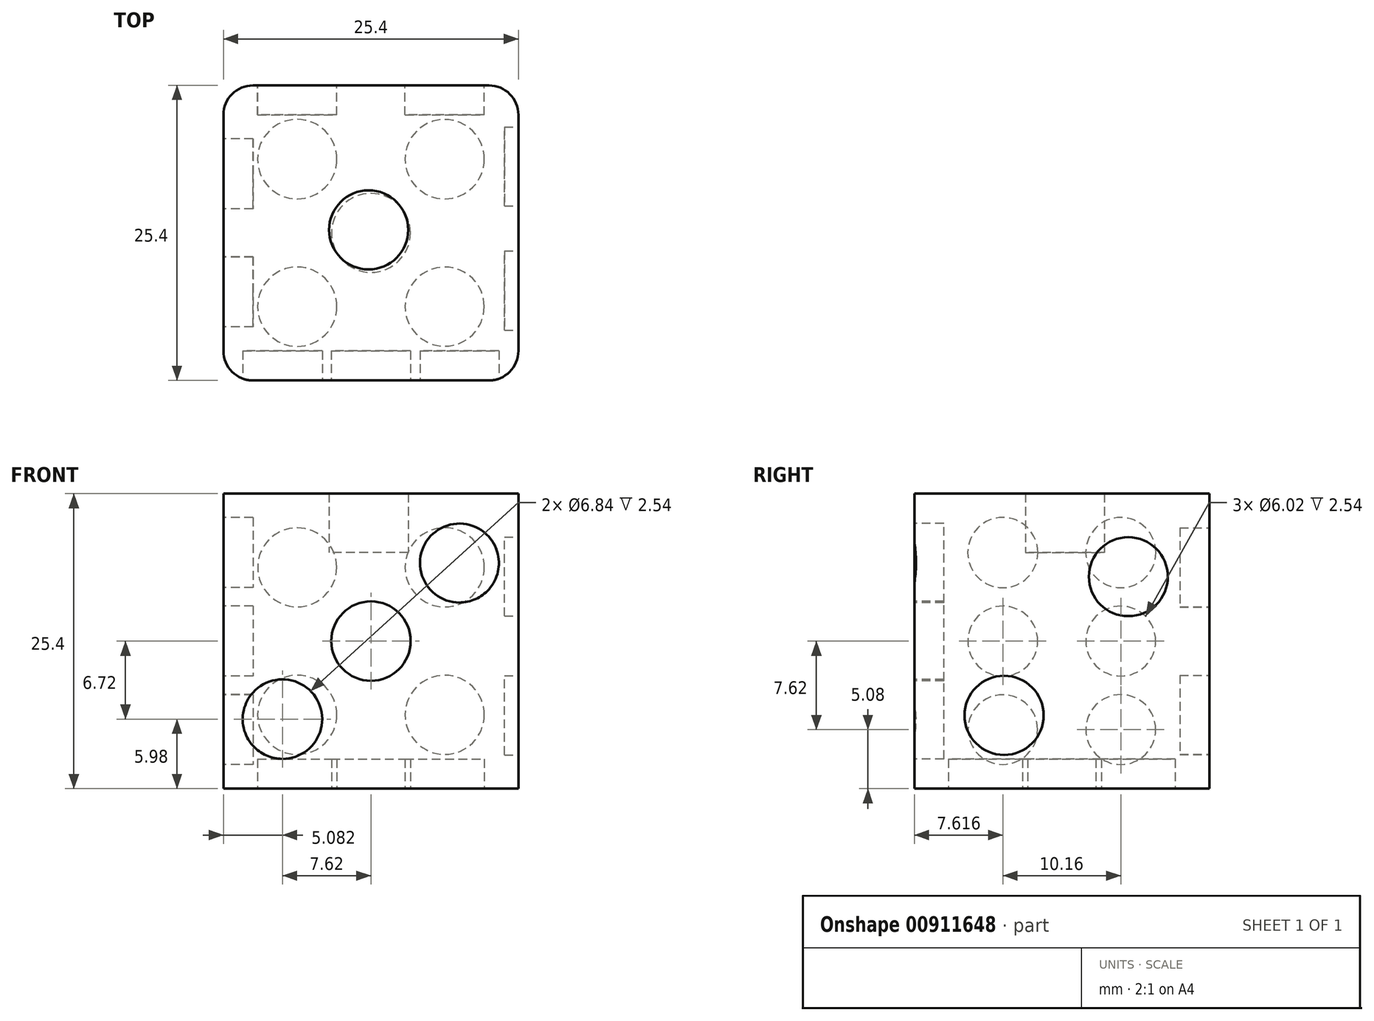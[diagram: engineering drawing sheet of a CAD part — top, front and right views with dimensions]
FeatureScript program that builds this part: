
annotation { "Feature Type Name" : "Feature", "Feature Type Description" : "" }
export const myFeature = defineFeature(function(context is Context, id is Id, definition is map)
    precondition{}
    {
        {
            var Q0;
            Q0=qCreatedBy(makeId("Top.planeOp"),FACE);
            var sketch = newSketch(context, id + "F0", { "sketchPlane" : qUnion([Q0])});
            skLineSegment(sketch, "E0.bottom", {"start": v(-22.93, 8.38) * mm, "end": v(-5.15, 8.38) * mm});
            skLineSegment(sketch, "E0.top", {"start": v(-22.93, -17.02) * mm, "end": v(-5.15, -17.02) * mm});
            skLineSegment(sketch, "E0.left", {"start": v(-26.74, 4.57) * mm, "end": v(-26.74, -13.21) * mm});
            skLineSegment(sketch, "E0.right", {"start": v(-1.34, 4.57) * mm, "end": v(-1.34, -13.21) * mm});
            skLineSegment(sketch, "E1.bottom", {"start": v(-15, 3.03) * mm, "end": v(-14.46, 3.03) * mm});
            skCircle(sketch, "E2", {"center": v(-14.24, -4.06) * mm, "radius": 3.4 * mm});
            skPoint(sketch, "E3.visualSharp", {"position": v(-26.74, 8.38) * mm});
            skPoint(sketch, "E4.visualSharp", {"position": v(-26.74, -17.02) * mm});
            skPoint(sketch, "E5.visualSharp", {"position": v(-1.34, -17.02) * mm});
            skPoint(sketch, "E6.visualSharp", {"position": v(-1.34, 8.38) * mm});
            skLineSegment(sketch, "E7", {"start": v(-26.74, -13.21) * mm, "end": v(-26.74, -14.48) * mm});
            skLineSegment(sketch, "E8", {"start": v(-24.2, -17.02) * mm, "end": v(-22.93, -17.02) * mm});
            skLineSegment(sketch, "E9", {"start": v(-1.34, -14.48) * mm, "end": v(-1.34, -13.21) * mm});
            skLineSegment(sketch, "E10", {"start": v(-5.15, -17.02) * mm, "end": v(-3.88, -17.02) * mm});
            skLineSegment(sketch, "E11", {"start": v(-1.34, 4.57) * mm, "end": v(-1.34, 5.84) * mm});
            skLineSegment(sketch, "E12", {"start": v(-4.55, 8.33) * mm, "end": v(-5.15, 8.38) * mm});
            skLineSegment(sketch, "E13", {"start": v(-3.88, 8.38) * mm, "end": v(-5.15, 8.38) * mm});
            skLineSegment(sketch, "E14", {"start": v(-22.93, 8.38) * mm, "end": v(-24.2, 8.38) * mm});
            skLineSegment(sketch, "E15", {"start": v(-26.74, 4.57) * mm, "end": v(-26.74, 5.84) * mm});
            skArc(sketch, "E16.filletArc", {"start": v(-24.2, 8.38) * mm, "mid": v(-26, 7.63) * mm, "end": v(-26.74, 5.84) * mm});
            skArc(sketch, "E17.filletArc", {"start": v(-1.34, 5.84) * mm, "mid": v(-2.08, 7.63) * mm, "end": v(-3.88, 8.38) * mm});
            skArc(sketch, "E18.filletArc", {"start": v(-3.88, -17.02) * mm, "mid": v(-2.08, -16.28) * mm, "end": v(-1.34, -14.48) * mm});
            skArc(sketch, "E19.filletArc", {"start": v(-26.74, -14.48) * mm, "mid": v(-26, -16.28) * mm, "end": v(-24.2, -17.02) * mm});
            skSolve(sketch);
        }
        {
            var Q0;
            Q0 = qSketchRegion(id + "F0", true);
            extrude(context, id + "F1", {"entities" : qUnion([Q0]), "depth" : 25.4 * mm, "offsetDistance" : 25.4 * mm});
        }
        {
            var Q0;
            Q0=qCreatedBy(makeId("Right.planeOp"),FACE);
            var sketch = newSketch(context, id + "F2", { "sketchPlane" : qUnion([Q0])});
            skCircle(sketch, "E20", {"center": v(-9.3, 6.3) * mm, "radius": 3.4 * mm});
            skCircle(sketch, "E21", {"center": v(1.4, 18.25) * mm, "radius": 3.4 * mm});
            skSolve(sketch);
        }
        {
            var Q0;
            Q0=makeQuery(id+"F0.imprint","IMPRINT",FACE,{"disambiguationData":[TD([[makeQuery(id+"F0.imprint","IMPRINT",EDGE,{"derivedFrom":sQuery(id+"F0.wireOp",EDGE,"E2")}),1.0]])]});
            extrude(context, id + "F3", {"entities" : qUnion([Q0]), "operationType" : NewBodyOperationType.ADD, "depth" : 20.32 * mm, "offsetDistance" : 25.4 * mm});
        }
        {
            var Q0;
            Q0=makeQuery(id+"F1.opExtrude","SWEPT_FACE",FACE,{"disambiguationData":[OSD([sQuery(id+"F0.wireOp",EDGE,"E0.top")])]});
            var sketch = newSketch(context, id + "F4", { "sketchPlane" : qUnion([Q0])});
            skCircle(sketch, "E22", {"center": v(-21.66, 5.98) * mm, "radius": 3.42 * mm});
            skCircle(sketch, "E23", {"center": v(-6.42, 19.42) * mm, "radius": 3.4 * mm});
            skCircle(sketch, "E24", {"center": v(-14.04, 12.7) * mm, "radius": 3.42 * mm});
            skSolve(sketch);
        }
        {
            var Q0;
            Q0=makeQuery(id+"F4.imprint","IMPRINT",FACE,{"disambiguationData":[TD([[makeQuery(id+"F4.imprint","IMPRINT",EDGE,{"derivedFrom":sQuery(id+"F4.wireOp",EDGE,"E22")}),1.0]])]});
            var Q1;
            Q1=makeQuery(id+"F4.imprint","IMPRINT",FACE,{"disambiguationData":[TD([[makeQuery(id+"F4.imprint","IMPRINT",EDGE,{"derivedFrom":sQuery(id+"F4.wireOp",EDGE,"E24")}),1.0]])]});
            var Q2;
            Q2=makeQuery(id+"F4.imprint","IMPRINT",FACE,{"disambiguationData":[TD([[makeQuery(id+"F4.imprint","IMPRINT",EDGE,{"derivedFrom":sQuery(id+"F4.wireOp",EDGE,"E23")}),1.0]])]});
            extrude(context, id + "F5", {"entities" : qUnion([Q0, Q1, Q2]), "operationType" : NewBodyOperationType.REMOVE, "oppositeDirection" : true, "depth" : 2.54 * mm, "offsetDistance" : 25.4 * mm});
        }
        {
            var Q0;
            Q0=makeQuery(id+"F1.opExtrude","SWEPT_FACE",FACE,{"disambiguationData":[OSD([sQuery(id+"F0.wireOp",EDGE,"E0.bottom")])]});
            var sketch = newSketch(context, id + "F6", { "sketchPlane" : qUnion([Q0])});
            skLineSegment(sketch, "E25", {"start": v(14.04, 25.4) * mm, "end": v(14.04, 0) * mm});
            skPoint(sketch, "E26.endSnap0", {"position": v(20.39, 19.05) * mm});
            skPoint(sketch, "E27.endSnap0", {"position": v(7.69, 6.35) * mm});
            skCircle(sketch, "E28", {"center": v(7.69, 6.35) * mm, "radius": 3.4 * mm});
            skCircle(sketch, "E29", {"center": v(20.39, 6.35) * mm, "radius": 3.4 * mm});
            skCircle(sketch, "E30", {"center": v(20.39, 19.05) * mm, "radius": 3.4 * mm});
            skCircle(sketch, "E31", {"center": v(7.69, 19.05) * mm, "radius": 3.4 * mm});
            skSolve(sketch);
        }
        {
            var Q0;
            Q0=makeQuery(id+"F6.imprint","IMPRINT",FACE,{"disambiguationData":[TD([[makeQuery(id+"F6.imprint","IMPRINT",EDGE,{"derivedFrom":sQuery(id+"F6.wireOp",EDGE,"E31")}),1.0]])]});
            var Q1;
            Q1=makeQuery(id+"F6.imprint","IMPRINT",FACE,{"disambiguationData":[TD([[makeQuery(id+"F6.imprint","IMPRINT",EDGE,{"derivedFrom":sQuery(id+"F6.wireOp",EDGE,"E29")}),1.0]])]});
            var Q2;
            Q2=makeQuery(id+"F6.imprint","IMPRINT",FACE,{"disambiguationData":[TD([[makeQuery(id+"F6.imprint","IMPRINT",EDGE,{"derivedFrom":sQuery(id+"F6.wireOp",EDGE,"E30")}),1.0]])]});
            var Q3;
            Q3=makeQuery(id+"F6.imprint","IMPRINT",FACE,{"disambiguationData":[TD([[makeQuery(id+"F6.imprint","IMPRINT",EDGE,{"derivedFrom":sQuery(id+"F6.wireOp",EDGE,"E28")}),1.0]])]});
            extrude(context, id + "F7", {"entities" : qUnion([Q0, Q1, Q2, Q3]), "operationType" : NewBodyOperationType.REMOVE, "oppositeDirection" : true, "depth" : 2.54 * mm, "offsetDistance" : 25.4 * mm});
        }
        {
            var Q0;
            {var subQ0=sQuery(id+"F0.wireOp",EDGE,"E2");Q0=makeQuery(id+"F3.boolean.opBoolean","MERGE",FACE,{"derivedFrom":[makeQuery(id+"F1.opExtrude","CAP_FACE",FACE,{"disambiguationData":[OSD([sQuery(id+"F0.wireOp",EDGE,"E0.bottom"),sQuery(id+"F0.wireOp",EDGE,"E0.top"),sQuery(id+"F0.wireOp",EDGE,"E0.left"),sQuery(id+"F0.wireOp",EDGE,"E0.right"),subQ0])],"isStart":true}),makeQuery(id+"F3.opExtrude","CAP_FACE",FACE,{"disambiguationData":[OSD([subQ0])],"isStart":true})]});}
            var sketch = newSketch(context, id + "F8", { "sketchPlane" : qUnion([Q0])});
            skPoint(sketch, "E32.oppositeSnap0", {"position": v(-26.74, 4.32) * mm});
            skCircle(sketch, "E33", {"center": v(-14.04, 4.32) * mm, "radius": 3.4 * mm});
            skPoint(sketch, "E34.endSnap0", {"position": v(-14.04, -8.38) * mm});
            skCircle(sketch, "E35", {"center": v(-20.39, 10.67) * mm, "radius": 3.42 * mm});
            skCircle(sketch, "E36", {"center": v(-7.69, 10.67) * mm, "radius": 3.4 * mm});
            skCircle(sketch, "E37", {"center": v(-7.69, -2.03) * mm, "radius": 3.42 * mm});
            skCircle(sketch, "E38", {"center": v(-20.39, -2.03) * mm, "radius": 3.42 * mm});
            skLineSegment(sketch, "E39", {"start": v(-14.04, 4.32) * mm, "end": v(-26.74, 4.32) * mm});
            skLineSegment(sketch, "E40", {"start": v(-20.39, 4.32) * mm, "end": v(-20.39, 17.02) * mm});
            skLineSegment(sketch, "E41", {"start": v(-20.39, 4.32) * mm, "end": v(-20.39, -8.38) * mm});
            skLineSegment(sketch, "E42", {"start": v(-14.04, 4.32) * mm, "end": v(-1.34, 4.32) * mm});
            skLineSegment(sketch, "E43", {"start": v(-7.69, 4.32) * mm, "end": v(-7.69, -8.38) * mm});
            skLineSegment(sketch, "E44", {"start": v(-7.69, 4.32) * mm, "end": v(-7.69, 17.02) * mm});
            skSolve(sketch);
        }
        {
            var Q0;
            Q0 = qSketchRegion(id + "F8", true);
            extrude(context, id + "F9", {"entities" : qUnion([Q0]), "operationType" : NewBodyOperationType.REMOVE, "oppositeDirection" : true, "depth" : 2.54 * mm, "offsetDistance" : 25.4 * mm});
        }
        {
            var Q0;
            Q0=makeQuery(id+"F1.opExtrude","SWEPT_FACE",FACE,{"disambiguationData":[OSD([sQuery(id+"F0.wireOp",EDGE,"E0.left")])]});
            var sketch = newSketch(context, id + "F10", { "sketchPlane" : qUnion([Q0])});
            skCircle(sketch, "E45", {"center": v(9.4, 20.32) * mm, "radius": 3.02 * mm});
            skCircle(sketch, "E46", {"center": v(-0.76, 5.08) * mm, "radius": 3.01 * mm});
            skCircle(sketch, "E47", {"center": v(-0.76, 12.7) * mm, "radius": 3 * mm});
            skCircle(sketch, "E48", {"center": v(9.4, 12.7) * mm, "radius": 3.01 * mm});
            skCircle(sketch, "E49", {"center": v(-0.76, 20.32) * mm, "radius": 3.02 * mm});
            skCircle(sketch, "E50", {"center": v(9.4, 5.08) * mm, "radius": 3 * mm});
            skSolve(sketch);
        }
        {
            var Q0;
            Q0=makeQuery(id+"F10.imprint","IMPRINT",FACE,{"disambiguationData":[TD([[makeQuery(id+"F10.imprint","IMPRINT",EDGE,{"derivedFrom":sQuery(id+"F10.wireOp",EDGE,"E45")}),1.0]])]});
            var Q1;
            Q1=makeQuery(id+"F10.imprint","IMPRINT",FACE,{"disambiguationData":[TD([[makeQuery(id+"F10.imprint","IMPRINT",EDGE,{"derivedFrom":sQuery(id+"F10.wireOp",EDGE,"E48")}),1.0]])]});
            var Q2;
            Q2=makeQuery(id+"F10.imprint","IMPRINT",FACE,{"disambiguationData":[TD([[makeQuery(id+"F10.imprint","IMPRINT",EDGE,{"derivedFrom":sQuery(id+"F10.wireOp",EDGE,"E47")}),1.0]])]});
            var Q3;
            Q3=makeQuery(id+"F10.imprint","IMPRINT",FACE,{"disambiguationData":[TD([[makeQuery(id+"F10.imprint","IMPRINT",EDGE,{"derivedFrom":sQuery(id+"F10.wireOp",EDGE,"E49")}),1.0]])]});
            var Q4;
            Q4=makeQuery(id+"F10.imprint","IMPRINT",FACE,{"disambiguationData":[TD([[makeQuery(id+"F10.imprint","IMPRINT",EDGE,{"derivedFrom":sQuery(id+"F10.wireOp",EDGE,"E46")}),1.0]])]});
            var Q5;
            Q5=makeQuery(id+"F10.imprint","IMPRINT",FACE,{"disambiguationData":[TD([[makeQuery(id+"F10.imprint","IMPRINT",EDGE,{"derivedFrom":sQuery(id+"F10.wireOp",EDGE,"E50")}),1.0]])]});
            extrude(context, id + "F11", {"entities" : qUnion([Q0, Q1, Q2, Q3, Q4, Q5]), "operationType" : NewBodyOperationType.REMOVE, "oppositeDirection" : true, "depth" : 2.54 * mm, "offsetDistance" : 25.4 * mm});
        }
        {
            var Q0;
            Q0=makeQuery(id+"F2.imprint","IMPRINT",FACE,{"disambiguationData":[TD([[makeQuery(id+"F2.imprint","IMPRINT",EDGE,{"derivedFrom":sQuery(id+"F2.wireOp",EDGE,"E20")}),1.0]])]});
            var Q1;
            Q1=makeQuery(id+"F2.imprint","IMPRINT",FACE,{"disambiguationData":[TD([[makeQuery(id+"F2.imprint","IMPRINT",EDGE,{"derivedFrom":sQuery(id+"F2.wireOp",EDGE,"E21")}),1.0]])]});
            extrude(context, id + "F12", {"entities" : qUnion([Q0, Q1]), "operationType" : NewBodyOperationType.REMOVE, "oppositeDirection" : true, "depth" : 2.54 * mm, "offsetDistance" : 25.4 * mm});
        }
    });
